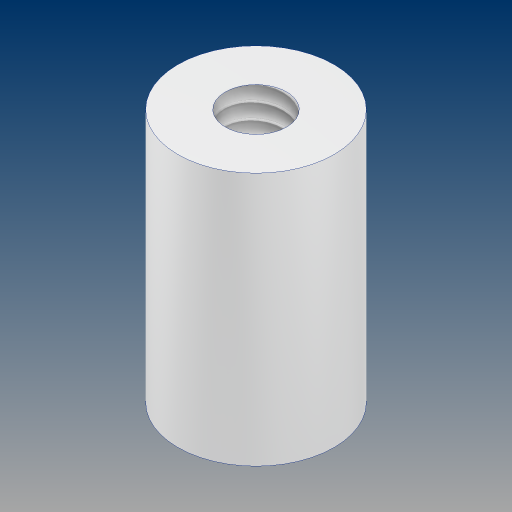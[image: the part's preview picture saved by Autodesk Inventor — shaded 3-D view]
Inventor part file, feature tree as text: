
AUTODESK INVENTOR PART (.ipt)
format: ipt  version: 2024.3 (Build 283343000, 343)  size: 126,464 bytes
history: native  units: in
note: dims shown in document units (in); Inventor stores cm internally (conversion verified against a paired STEP export)
features: sketch x2, extrude x1, hole x1
ambient origin geometry x8: Origin, YZ Plane, XZ Plane, XY Plane, X Axis, Y Axis, Z Axis, Center Point
bodies: Solid1 (feature_tree)
feature tree (4):
  extrude  "Extrusion1"  Depth=0.813in TaperAngle=0.0deg
  hole  "Hole1"  [1 undecoded]
  sketch  "Sketch1"  dims[d0=0.5in d1=0.813in d2=0.0in]
  sketch  "Sketch2"  dims[d3=0.196in d4=1.0in d5=0.375in d6=0.25in d7=0.5635in d8=1.0in d9=0.8108in]
note: 1 required parameter value undecoded (feature->parameter linkage not recoverable at this tier; creation-order binding heuristic only, values carry confidence <= 0.55)
